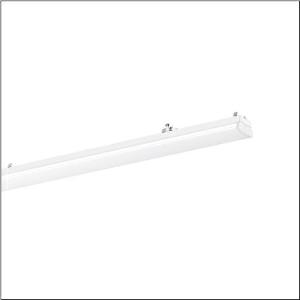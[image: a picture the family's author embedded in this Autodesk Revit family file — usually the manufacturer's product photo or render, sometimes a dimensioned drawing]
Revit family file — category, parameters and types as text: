
# Revit family: licross_r__21_recessed_opal_mo_52tl1dmn4axg_843c
name_source: partatom
category: Lighting Fixtures
units: mm (PartAtom-declared; Revit-internal decimal feet)

## family parameters
Cut with Voids When Loaded = No
Host = Face
Light Source = No
Part Type = Normal
Room Calculation Point = No
Round Connector Dimension = Use Diameter
Shared = No

## types (1)
- --- (1 x LED, 10420 lm, 60.5 W, 4000K)
    Apparent Load = 61 VA
    CIE Flux Codes = 44 73 91 87 100
    Color Rendering = 80
    Color Temperature = 4000K
    Default Elevation = 1800 mm
    Description = Licross® 21 recessed opal MO, luminaire insert, of sheet steel, galvanised, coil coated, white, length: 1.500mm, width: 66mm, height: 67mm, LED rated luminous flux: 10.420lm, light colour: 840, control gear: ON/OFF Multilumen, with plug, 3-pole, with phase selection, mains connection: 220..240V, AC, 50/60Hz, rated input power: 61W, halogen-free wiring, primary optical cover: cover, of PMMA, light emission: direct with ceiling illumination distribution, primary light characteristic: symmetric, protection rating (complete): IP40, insulation class (complete): insulation class I (protective earthing), certification: CE, ENEC, VDE, UKCA, protection symbol: D if used in an environment without relevant dust loads with corresponding accessories, impact resistance: IK06, permissible ambient temperature for indoor applications: -35..+40°C, corresponds to IFS (International Featured Standards) requirements for safety and quality in the food industry, reducing of maximum allowable ambient temperature of 5°C with ceiling mounting, LABS conformity tested according to VDMA 24364:2018-05, packaging unit: 1 piece
    Height = 83 mm
    Lamp = 1 x LED
    Lamp Light Flux = 10420 lm
    Lamp Power = 60.5 W
    Lamp count = 1
    Length = 1500 mm
    Luminous efficacy = 172 lm/W
    Manufacturer = Siteco
    ModVariant = No
    Model = 52TL1DMN4AXG
    Mounting Place = Ceiling
    Mounting Type = Pendant
    Number of Poles = 1
    OnlyDefault = Yes
    Power Factor = 1
    Product Name = Licross® 21 recessed opal MO
    Product group = luminaire insert
    ProductGroupID = 901
    Protection Class = Protection class I
    Protection Degree = IP 40
    RLX_Detail_Level = 1
    RLX_Emergency_Light_Flux = 0 lm
    RLX_Emergency_Type = 0
    RLX_Emergency_Type_DB = No
    RlxData = <blob elided: 24473 chars, md5=ec2996b1>
    Socket = socket
    Standby Power = 0 W
    System Light Flux = 10420 lm
    System Power = 61 W
    Type Comments = factory setting: luminous flux: 100 % | (A | C | E) | 140 mA
    Type Image = l_1313666.jpg
    URL = http://relux.com
    VarID = @adj_023371
    Voltage = 0 V
    Weight = 0.00 kg
    Width = 76 mm

## geometry (parser evidence)
native form markers: Blend x4, Sweep x13
no freeform markers — native parametric forms only
